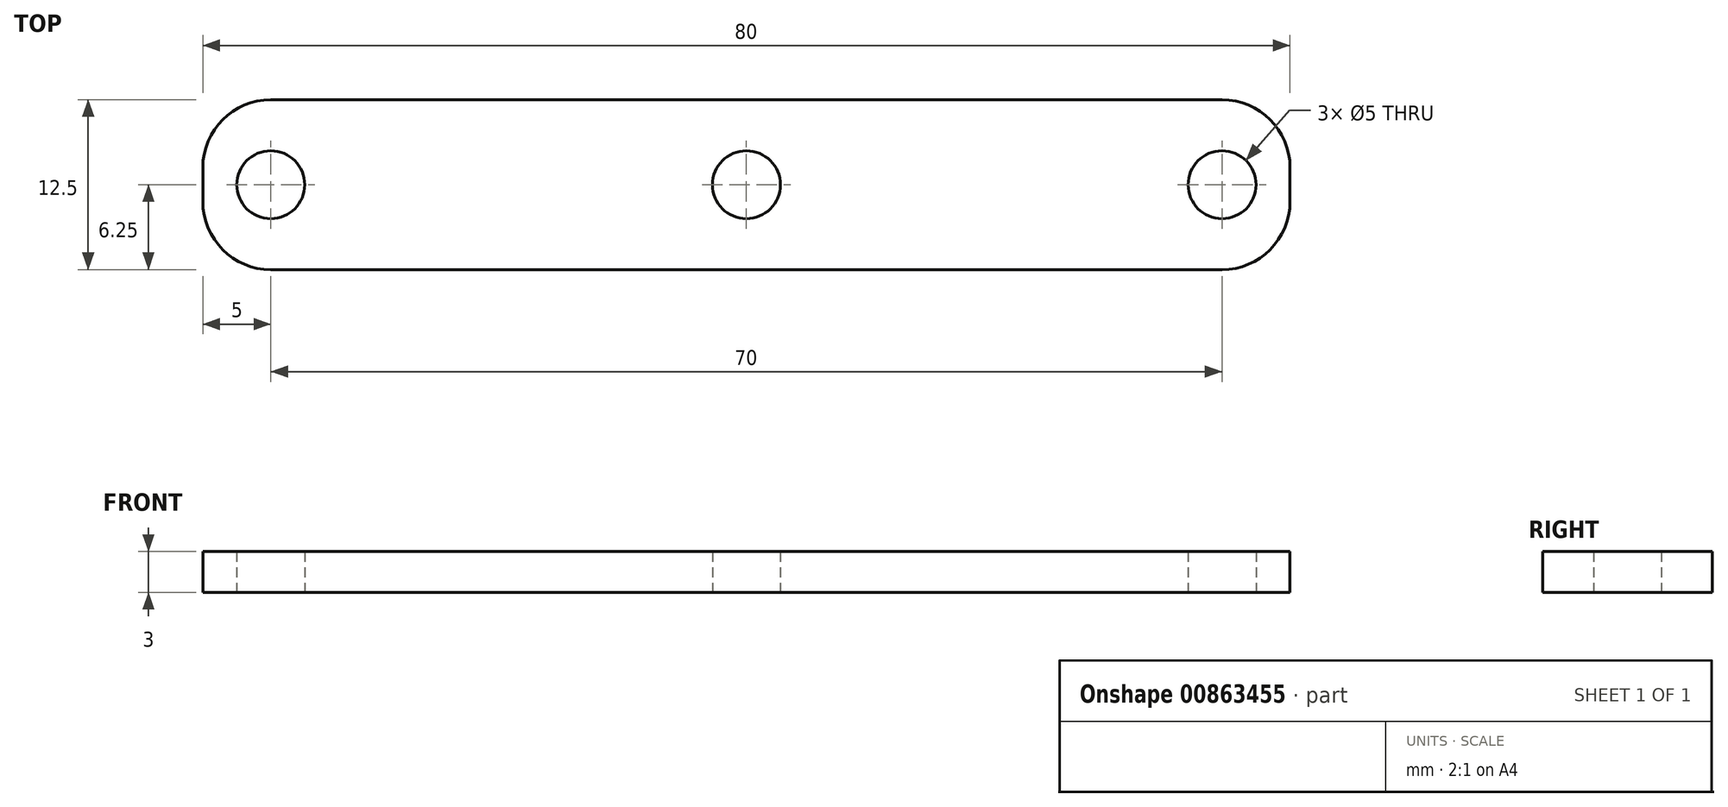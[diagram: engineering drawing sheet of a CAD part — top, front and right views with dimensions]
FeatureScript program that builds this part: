
annotation { "Feature Type Name" : "Feature", "Feature Type Description" : "" }
export const myFeature = defineFeature(function(context is Context, id is Id, definition is map)
    precondition{}
    {
        {
            var Q0;
            Q0=qCreatedBy(makeId("Top.planeOp"),FACE);
            var sketch = newSketch(context, id + "F0", { "sketchPlane" : qUnion([Q0])});
            skLineSegment(sketch, "E0.bottom", {"start": v(40, -6.25) * mm, "end": v(-40, -6.25) * mm});
            skLineSegment(sketch, "E0.top", {"start": v(40, 6.25) * mm, "end": v(-40, 6.25) * mm});
            skLineSegment(sketch, "E0.left", {"start": v(40, -6.25) * mm, "end": v(40, 6.25) * mm});
            skLineSegment(sketch, "E0.right", {"start": v(-40, -6.25) * mm, "end": v(-40, 6.25) * mm});
            skPoint(sketch, "E0.middle", {"position": v(0, 0) * mm});
            skSolve(sketch);
        }
        {
            var Q0;
            Q0=makeQuery(id+"F0.imprint","IMPRINT",FACE,{"disambiguationData":[TD([[makeQuery(id+"F0.imprint","IMPRINT",EDGE,{"derivedFrom":sQuery(id+"F0.wireOp",EDGE,"E0.bottom")}),-1.0]])]});
            extrude(context, id + "F1", {"entities" : qUnion([Q0]), "depth" : 3 * mm, "offsetDistance" : 25 * mm});
        }
        {
            var Q0;
            Q0=makeQuery(id+"F1.opExtrude","SWEPT_EDGE",EDGE,{"disambiguationData":[OSD([sQuery(id+"F0.wireOp",EDGE,"E0.bottom"),sQuery(id+"F0.wireOp",EDGE,"E0.left")])]});
            var Q1;
            Q1=makeQuery(id+"F1.opExtrude","SWEPT_EDGE",EDGE,{"disambiguationData":[OSD([sQuery(id+"F0.wireOp",EDGE,"E0.top"),sQuery(id+"F0.wireOp",EDGE,"E0.left")])]});
            var Q2;
            Q2=makeQuery(id+"F1.opExtrude","SWEPT_EDGE",EDGE,{"disambiguationData":[OSD([sQuery(id+"F0.wireOp",EDGE,"E0.bottom"),sQuery(id+"F0.wireOp",EDGE,"E0.right")])]});
            var Q3;
            Q3=makeQuery(id+"F1.opExtrude","SWEPT_EDGE",EDGE,{"disambiguationData":[OSD([sQuery(id+"F0.wireOp",EDGE,"E0.top"),sQuery(id+"F0.wireOp",EDGE,"E0.right")])]});
            fillet(context, id + "F2", {"entities" : qUnion([Q0, Q1, Q2, Q3]), "radius" : 5 * mm, "tangentPropagation" : true, "allowEdgeOverflow" : false});
        }
        {
            var Q0;
            Q0=makeQuery(id+"F1.opExtrude","CAP_FACE",FACE,{"disambiguationData":[OSD([sQuery(id+"F0.wireOp",EDGE,"E0.bottom"),sQuery(id+"F0.wireOp",EDGE,"E0.top"),sQuery(id+"F0.wireOp",EDGE,"E0.left"),sQuery(id+"F0.wireOp",EDGE,"E0.right")])],"isStart":true});
            var sketch = newSketch(context, id + "F3", { "sketchPlane" : qUnion([Q0])});
            skCircle(sketch, "E1", {"center": v(-35, 0) * mm, "radius": 2.5 * mm});
            skCircle(sketch, "E2", {"center": v(35, 0) * mm, "radius": 2.5 * mm});
            skCircle(sketch, "E3", {"center": v(0, 0) * mm, "radius": 2.5 * mm});
            skSolve(sketch);
        }
        {
            var Q0;
            Q0=sQuery(id+"F3.wireOp",VERTEX,"E1.center");
            var Q1;
            Q1=sQuery(id+"F3.wireOp",VERTEX,"E3.center");
            var Q2;
            Q2=sQuery(id+"F3.wireOp",VERTEX,"E2.center");
            var Q3;
            Q3=makeQuery(id+"F1.opExtrude","SWEPT_BODY",BODY,{"disambiguationData":[OSD([sQuery(id+"F0.wireOp",EDGE,"E0.bottom"),sQuery(id+"F0.wireOp",EDGE,"E0.top"),sQuery(id+"F0.wireOp",EDGE,"E0.left"),sQuery(id+"F0.wireOp",EDGE,"E0.right")])]});
            hole(context, id + "F4", {"style" : HoleStyle.SIMPLE, "endStyle" : HoleEndStyle.THROUGH, "holeDiameter" : 5 * mm, "majorDiameter" : 5 * mm, "isTappedThrough" : true, "tappedDepth" : 12 * mm, "tapClearance" : 3, "locations" : qUnion([Q0, Q1, Q2]), "scope" : qUnion([Q3])});
        }
    });
